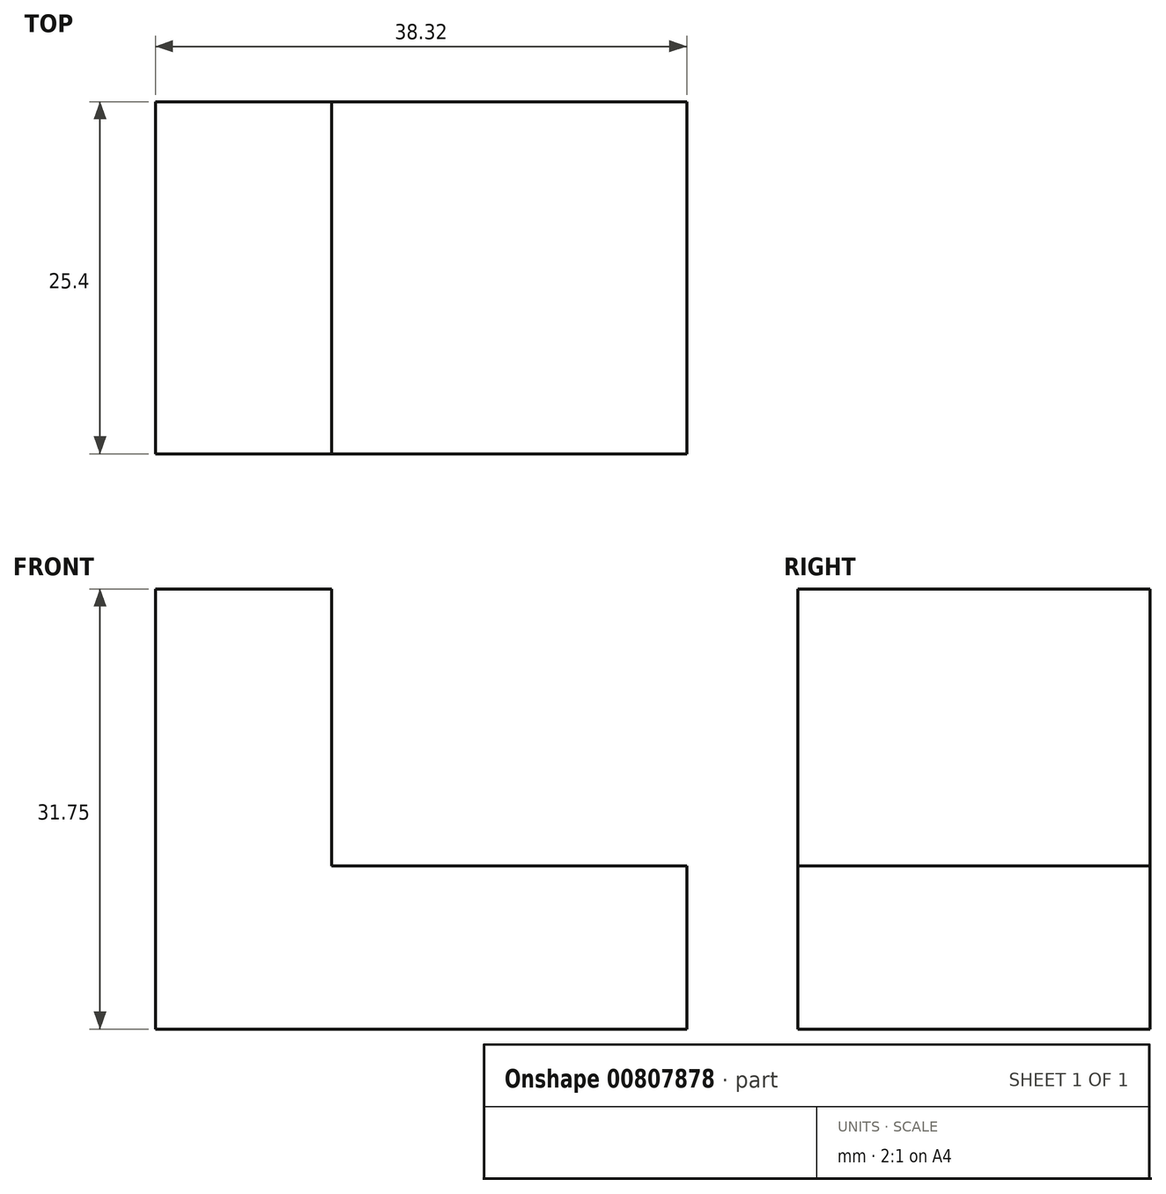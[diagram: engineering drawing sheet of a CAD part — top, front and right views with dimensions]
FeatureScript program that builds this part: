
annotation { "Feature Type Name" : "Feature", "Feature Type Description" : "" }
export const myFeature = defineFeature(function(context is Context, id is Id, definition is map)
    precondition{}
    {
        {
            var Q0;
            Q0=qCreatedBy(makeId("Front.planeOp"),FACE);
            var sketch = newSketch(context, id + "F0", { "sketchPlane" : qUnion([Q0])});
            skLineSegment(sketch, "E0", {"start": v(0, 0) * mm, "end": v(0, 31.75) * mm});
            skLineSegment(sketch, "E1", {"start": v(0, 31.75) * mm, "end": v(12.7, 31.75) * mm});
            skLineSegment(sketch, "E2", {"start": v(12.7, 31.75) * mm, "end": v(12.7, 11.76) * mm});
            skLineSegment(sketch, "E3", {"start": v(12.7, 11.76) * mm, "end": v(38.32, 11.76) * mm});
            skLineSegment(sketch, "E4", {"start": v(38.32, 11.76) * mm, "end": v(38.32, 0) * mm});
            skLineSegment(sketch, "E5", {"start": v(0, 0) * mm, "end": v(38.32, 0) * mm});
            skSolve(sketch);
        }
        {
            var Q0;
            Q0 = qSketchRegion(id + "F0", true);
            extrude(context, id + "F1", {"entities" : qUnion([Q0]), "oppositeDirection" : true, "depth" : 25.4 * mm, "offsetDistance" : 25.4 * mm});
        }
    });
